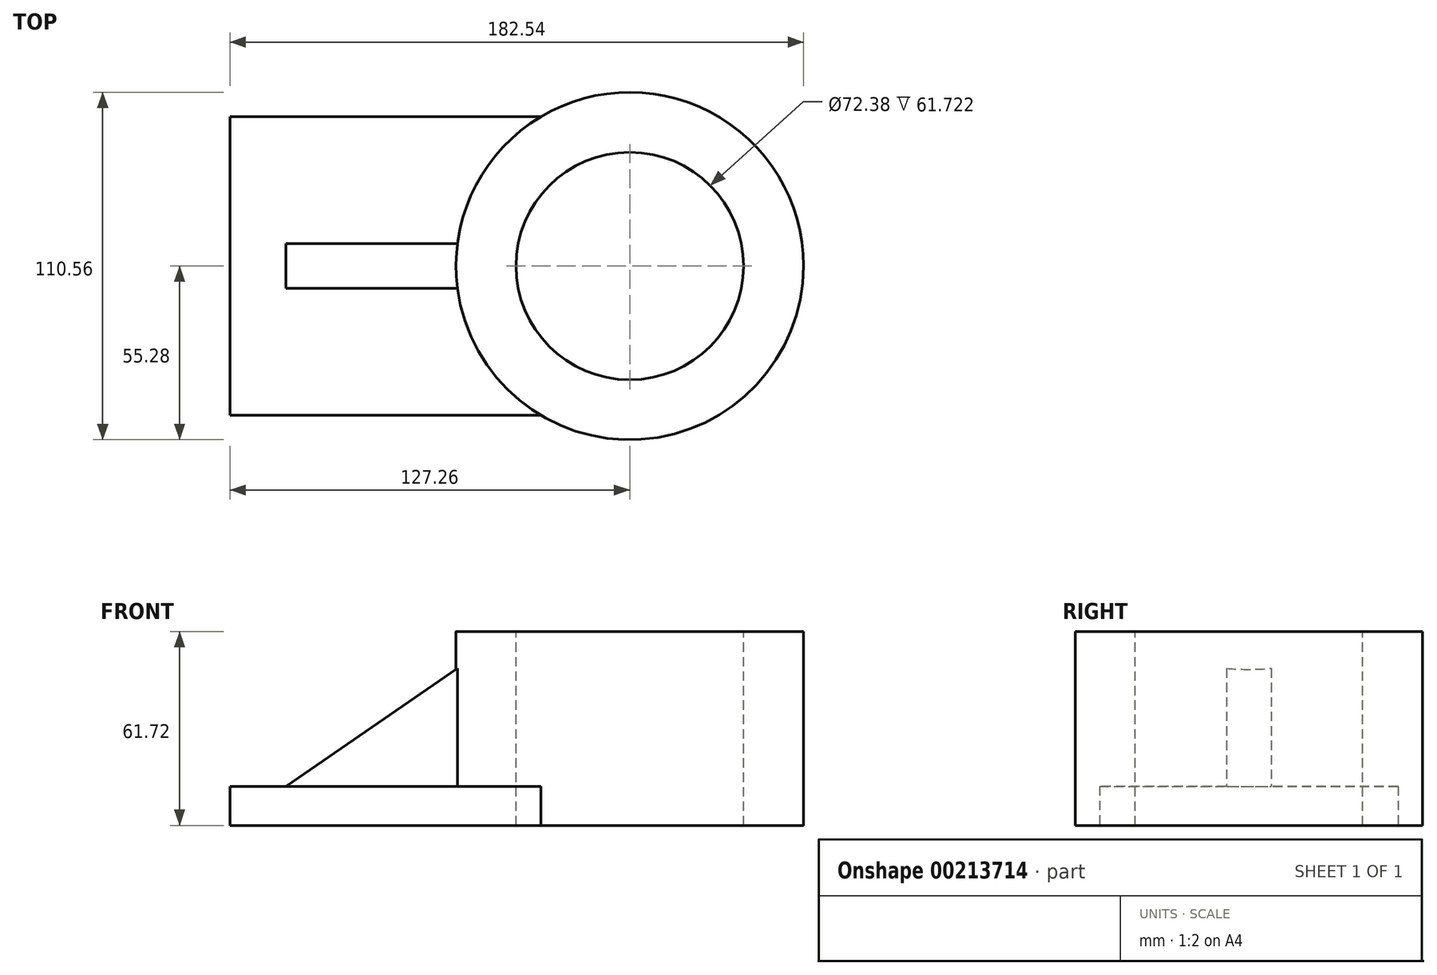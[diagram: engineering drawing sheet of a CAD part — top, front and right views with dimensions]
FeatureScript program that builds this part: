
annotation { "Feature Type Name" : "Feature", "Feature Type Description" : "" }
export const myFeature = defineFeature(function(context is Context, id is Id, definition is map)
    precondition{}
    {
        {
            var Q0;
            Q0=qCreatedBy(makeId("Top.planeOp"),FACE);
            var sketch = newSketch(context, id + "F0", { "sketchPlane" : qUnion([Q0])});
            skLineSegment(sketch, "E0.bottom", {"start": v(71.98, -47.5) * mm, "end": v(-71.98, -47.5) * mm});
            skLineSegment(sketch, "E0.top", {"start": v(71.98, 47.5) * mm, "end": v(-71.98, 47.5) * mm});
            skLineSegment(sketch, "E0.left", {"start": v(71.98, -47.5) * mm, "end": v(71.98, 47.5) * mm});
            skLineSegment(sketch, "E0.right", {"start": v(-71.98, -47.5) * mm, "end": v(-71.98, 47.5) * mm});
            skPoint(sketch, "E0.middle", {"position": v(0, 0) * mm});
            skSolve(sketch);
        }
        {
            var Q0;
            Q0 = qSketchRegion(id + "F0", true);
            extrude(context, id + "F1", {"entities" : qUnion([Q0]), "depth" : 12.45 * mm});
        }
        {
            var Q0;
            Q0=qCreatedBy(makeId("Top.planeOp"),FACE);
            var sketch = newSketch(context, id + "F2", { "sketchPlane" : qUnion([Q0])});
            skCircle(sketch, "E1", {"center": v(55.28, 0) * mm, "radius": 55.28 * mm});
            skSolve(sketch);
        }
        {
            var Q0;
            Q0=makeQuery(id+"F2.imprint","IMPRINT",FACE,{"disambiguationData":[TD([[makeQuery(id+"F2.imprint","IMPRINT",EDGE,{"derivedFrom":sQuery(id+"F2.wireOp",EDGE,"E1")}),1.0]])]});
            extrude(context, id + "F3", {"entities" : qUnion([Q0]), "operationType" : NewBodyOperationType.ADD, "depth" : 61.72 * mm});
        }
        {
            var Q0;
            Q0=makeQuery(id+"F3.opExtrude","CAP_FACE",FACE,{"disambiguationData":[OSD([sQuery(id+"F2.wireOp",EDGE,"E1")])],"isStart":false});
            var sketch = newSketch(context, id + "F4", { "sketchPlane" : qUnion([Q0])});
            skCircle(sketch, "E2", {"center": v(55.28, 0) * mm, "radius": 36.2 * mm});
            skSolve(sketch);
        }
        {
            var Q0;
            Q0 = qSketchRegion(id + "F4", true);
            extrude(context, id + "F5", {"entities" : qUnion([Q0]), "operationType" : NewBodyOperationType.REMOVE, "endBound" : BoundingType.THROUGH_ALL, "oppositeDirection" : true, "depth" : 25.4 * mm});
        }
        {
            var Q0;
            Q0=qCreatedBy(makeId("Front.planeOp"),FACE);
            var sketch = newSketch(context, id + "F6", { "sketchPlane" : qUnion([Q0])});
            skLineSegment(sketch, "E3", {"start": v(9.26, 56.01) * mm, "end": v(-61.7, 7.27) * mm});
            skLineSegment(sketch, "E4", {"start": v(-61.7, 7.27) * mm, "end": v(9.26, 7.27) * mm});
            skLineSegment(sketch, "E5", {"start": v(9.26, 7.27) * mm, "end": v(9.26, 56.01) * mm});
            skSolve(sketch);
        }
        {
            var Q0;
            Q0 = qSketchRegion(id + "F6", true);
            extrude(context, id + "F7", {"entities" : qUnion([Q0]), "operationType" : NewBodyOperationType.ADD, "depth" : 14.22 * mm, "symmetric" : true});
        }
    });
